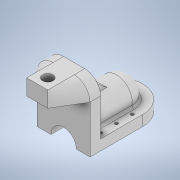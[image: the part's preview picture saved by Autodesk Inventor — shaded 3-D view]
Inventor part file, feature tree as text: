
AUTODESK INVENTOR PART (.ipt)
format: ipt  version: 2021 (Build 250183000, 183)  size: 252,928 bytes
history: native  units: mm
features: sketch x9, extrude x7, fillet x3, plane x2, loft x1
ambient origin geometry x8: Origin, YZ Plane, XZ Plane, XY Plane, X Axis, Y Axis, Z Axis, Center Point
bodies: Solid1 (feature_tree)
feature tree (22):
  extrude  "Extrusion1"  Depth=40.0mm
  extrude  "Extrusion2"  Depth=10.0mm
  extrude  "Extrusion3"  Depth=10.0mm
  fillet  "Fillet1"  Radius=50.0mm
  fillet  "Fillet2"  Radius=15.0mm
  sketch  "Sketch4"  dims[d9=10.0mm d10=0.0mm d11=30.0mm]
  extrude  "Extrusion4"  Depth=10.0mm
  plane  "Work Plane1"
  extrude  "Extrusion6"  Depth=55.0mm TaperAngle=0.0deg
  sketch  "Sketch8"  dims[d17=24.0mm d18=3.0mm]
  plane  "Work Plane2"
  loft  "Loft1"
  extrude  "Extrusion7"  Depth=3.0mm
  extrude  "Extrusion8"  Depth=5.0mm
  fillet  "Fillet3"  Radius=15.0mm
  sketch  "Sketch1"  dims[d0=50.0mm d1=40.0mm]
  sketch  "Sketch2"  dims[d2=10.0mm d3=50.0mm]
  sketch  "Sketch3"  dims[d4=10.0mm d5=0.0mm d6=50.0mm d7=50.0mm d8=15.0mm]
  sketch  "Sketch5"  dims[d12=15.0mm d13=55.0mm d14=0.0mm]
  sketch  "Sketch7"  dims[d15=15.0mm d16=2.0mm]
  sketch  "Sketch9"  dims[d19=5.0mm d20=5.0mm d21=15.0mm]
  sketch  "Sketch10"  dims[d22=30.0mm d24=15.0mm d25=10.0mm d27=10.0mm d29=62.0mm d30=0.0mm d31=-25.0mm d43=25.0mm d44=4.0mm d45=5.0mm d46=20.0mm d47=10.0mm d48=0.0mm d49=15.0mm d50=15.0mm d51=25.0mm d52=20.0mm d53=15.0mm d54=0.0mm d55=90.0deg d56=0.0mm d57=90.0deg d58=10.0mm d59=10.0mm d60=10.0mm d61=62.0mm d62=0.0mm d63=62.0mm d64=0.0mm d65=12.0mm]
